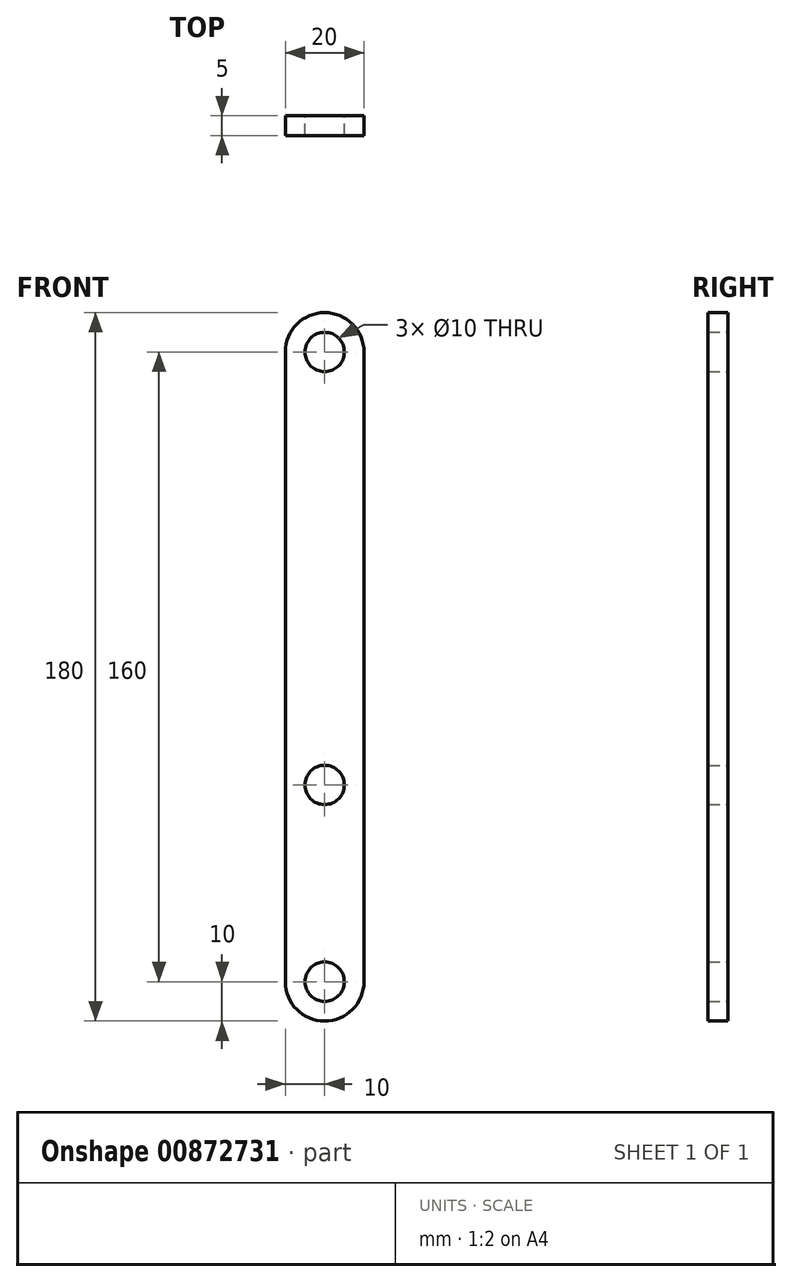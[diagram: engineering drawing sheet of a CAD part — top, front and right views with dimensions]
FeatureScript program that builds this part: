
annotation { "Feature Type Name" : "Feature", "Feature Type Description" : "" }
export const myFeature = defineFeature(function(context is Context, id is Id, definition is map)
    precondition{}
    {
        {
            var Q0;
            Q0=qCreatedBy(makeId("Front.planeOp"),FACE);
            var sketch = newSketch(context, id + "F0", { "sketchPlane" : qUnion([Q0])});
            skLineSegment(sketch, "E0.bottom", {"start": v(-10, 0) * mm, "end": v(10, 0) * mm});
            skLineSegment(sketch, "E0.top", {"start": v(-10, -160) * mm, "end": v(10, -160) * mm});
            skLineSegment(sketch, "E0.left", {"start": v(-10, 0) * mm, "end": v(-10, -160) * mm});
            skLineSegment(sketch, "E0.right", {"start": v(10, 0) * mm, "end": v(10, -160) * mm});
            skCircle(sketch, "E1", {"center": v(0, -160) * mm, "radius": 10 * mm});
            skCircle(sketch, "E2", {"center": v(0, 0) * mm, "radius": 10 * mm});
            skCircle(sketch, "E3", {"center": v(0, -110) * mm, "radius": 5 * mm});
            skCircle(sketch, "E4", {"center": v(0, 0) * mm, "radius": 5 * mm});
            skCircle(sketch, "E5", {"center": v(0, -160) * mm, "radius": 5 * mm});
            skSolve(sketch);
        }
        {
            var Q0;
            {var subQ1=sQuery(id+"F0.wireOp",EDGE,"E0.bottom");var subQ3=sQuery(id+"F0.wireOp",EDGE,"E4");var subQ4=makeQuery(id+"F0.imprint","INTERSECT",VERTEX,{"disambiguationData":[OD(0.0)],"derivedFrom":[subQ1,subQ3]});Q0=makeQuery(id+"F0.imprint","IMPRINT",FACE,{"disambiguationData":[TD([[makeQuery(id+"F0.imprint","IMPRINT",EDGE,{"disambiguationData":[TD([[subQ4,1.0]])],"derivedFrom":subQ3}),-1.0]])]});}
            var Q1;
            {var subQ1=sQuery(id+"F0.wireOp",EDGE,"E0.bottom");var subQ3=sQuery(id+"F0.wireOp",EDGE,"E4");var subQ4=makeQuery(id+"F0.imprint","INTERSECT",VERTEX,{"disambiguationData":[OD(0.0)],"derivedFrom":[subQ1,subQ3]});Q1=makeQuery(id+"F0.imprint","IMPRINT",FACE,{"disambiguationData":[TD([[makeQuery(id+"F0.imprint","IMPRINT",EDGE,{"disambiguationData":[TD([[subQ4,-1.0]])],"derivedFrom":subQ3}),-1.0]])]});}
            var Q2;
            {var subQ1=sQuery(id+"F0.wireOp",EDGE,"E0.left");Q2=makeQuery(id+"F0.imprint","IMPRINT",FACE,{"disambiguationData":[TD([[makeQuery(id+"F0.imprint","IMPRINT",EDGE,{"derivedFrom":subQ1}),1.0]])]});}
            var Q3;
            {var subQ1=sQuery(id+"F0.wireOp",EDGE,"E0.top");var subQ3=sQuery(id+"F0.wireOp",EDGE,"E5");var subQ4=makeQuery(id+"F0.imprint","INTERSECT",VERTEX,{"disambiguationData":[OD(0.0)],"derivedFrom":[subQ1,subQ3]});Q3=makeQuery(id+"F0.imprint","IMPRINT",FACE,{"disambiguationData":[TD([[makeQuery(id+"F0.imprint","IMPRINT",EDGE,{"disambiguationData":[TD([[subQ4,1.0]])],"derivedFrom":subQ3}),-1.0]])]});}
            var Q4;
            {var subQ1=sQuery(id+"F0.wireOp",EDGE,"E0.top");var subQ3=sQuery(id+"F0.wireOp",EDGE,"E5");var subQ4=makeQuery(id+"F0.imprint","INTERSECT",VERTEX,{"disambiguationData":[OD(0.0)],"derivedFrom":[subQ1,subQ3]});Q4=makeQuery(id+"F0.imprint","IMPRINT",FACE,{"disambiguationData":[TD([[makeQuery(id+"F0.imprint","IMPRINT",EDGE,{"disambiguationData":[TD([[subQ4,-1.0]])],"derivedFrom":subQ3}),-1.0]])]});}
            extrude(context, id + "F1", {"entities" : qUnion([Q0, Q1, Q2, Q3, Q4]), "depth" : 5 * mm, "offsetDistance" : 25 * mm});
        }
    });
